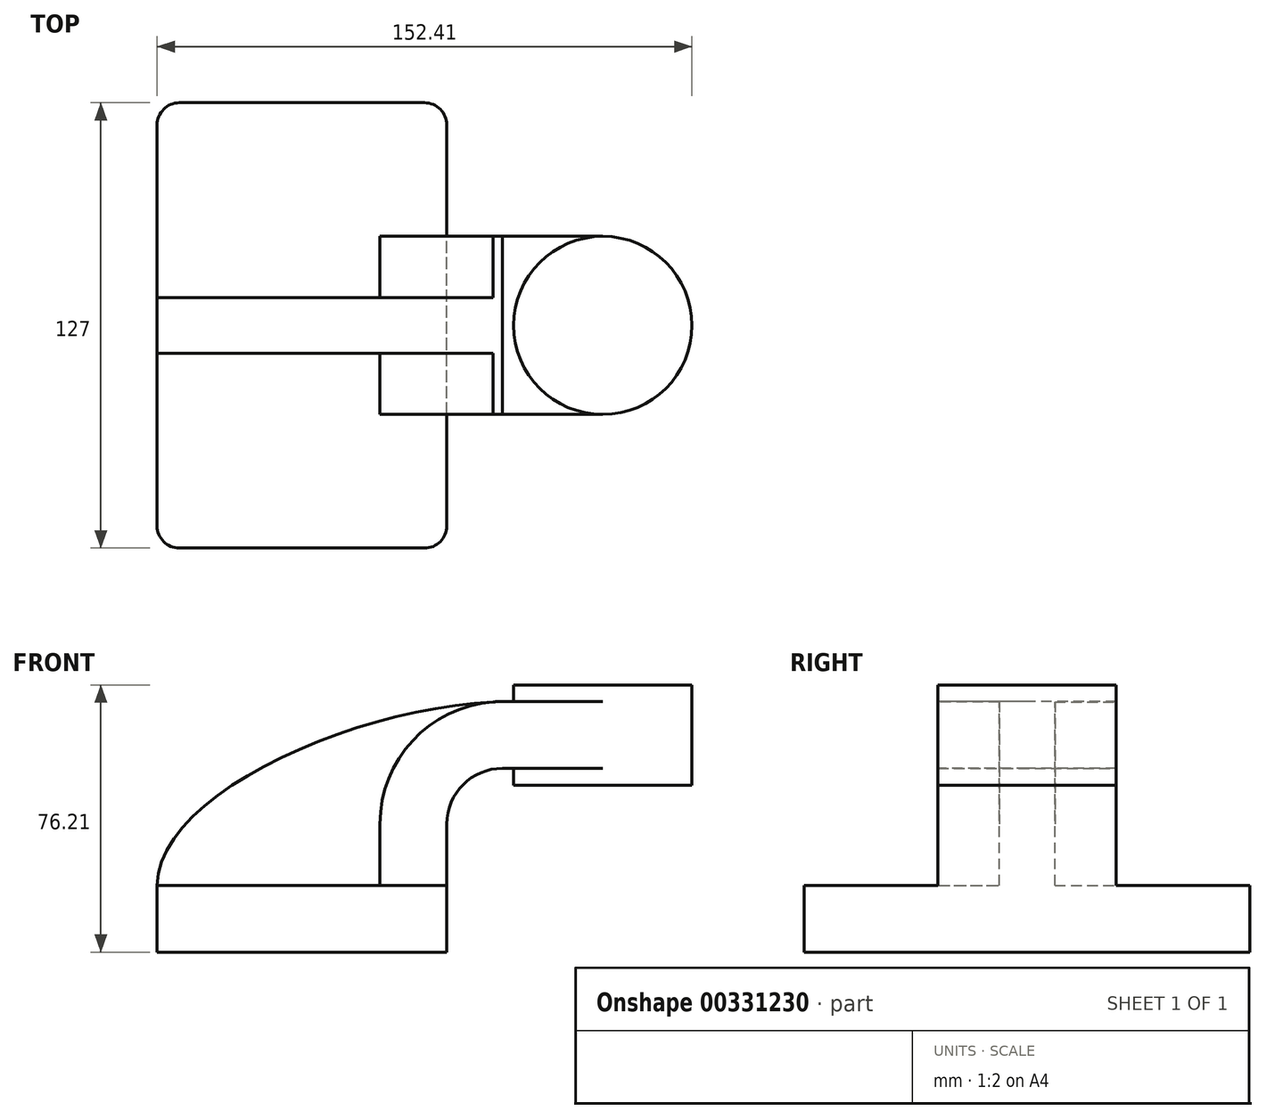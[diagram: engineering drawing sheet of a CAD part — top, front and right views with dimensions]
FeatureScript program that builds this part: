
annotation { "Feature Type Name" : "Feature", "Feature Type Description" : "" }
export const myFeature = defineFeature(function(context is Context, id is Id, definition is map)
    precondition{}
    {
        {
            var Q0;
            Q0=qCreatedBy(makeId("Front.planeOp"),FACE);
            var sketch = newSketch(context, id + "F0", { "sketchPlane" : qUnion([Q0])});
            skLineSegment(sketch, "E0.bottom", {"start": v(-41.27, 9.52) * mm, "end": v(41.28, 9.53) * mm});
            skLineSegment(sketch, "E0.top", {"start": v(-41.27, -9.53) * mm, "end": v(41.28, -9.53) * mm});
            skLineSegment(sketch, "E0.left", {"start": v(-41.28, 9.52) * mm, "end": v(-41.27, -9.53) * mm});
            skLineSegment(sketch, "E0.right", {"start": v(41.27, 9.53) * mm, "end": v(41.28, -9.52) * mm});
            skPoint(sketch, "E0.middle", {"position": v(0, 0) * mm});
            skLineSegment(sketch, "E1", {"start": v(41.27, 9.53) * mm, "end": v(41.27, 27) * mm});
            skLineSegment(sketch, "E2.bottom", {"start": v(60.32, 66.67) * mm, "end": v(111.12, 66.67) * mm});
            skLineSegment(sketch, "E2.top", {"start": v(60.33, 38.1) * mm, "end": v(111.12, 38.1) * mm});
            skLineSegment(sketch, "E2.left", {"start": v(60.32, 66.67) * mm, "end": v(60.33, 38.1) * mm});
            skLineSegment(sketch, "E2.right", {"start": v(111.12, 66.67) * mm, "end": v(111.12, 38.1) * mm});
            skPoint(sketch, "E2.middle", {"position": v(85.72, 52.39) * mm});
            skArc(sketch, "E3", {"start": v(57.15, 42.88) * mm, "mid": v(45.92, 38.23) * mm, "end": v(41.28, 27) * mm});
            skLineSegment(sketch, "E4", {"start": v(57.15, 42.88) * mm, "end": v(85.72, 42.88) * mm});
            skPoint(sketch, "E5", {"position": v(85.72, 38.1) * mm});
            skLineSegment(sketch, "E6.0", {"start": v(57.15, 61.93) * mm, "end": v(85.72, 61.93) * mm});
            skArc(sketch, "E6.1", {"start": v(57.15, 61.93) * mm, "mid": v(32.45, 51.7) * mm, "end": v(22.23, 27) * mm});
            skLineSegment(sketch, "E6.2", {"start": v(22.22, 9.53) * mm, "end": v(22.22, 27) * mm});
            skLineSegment(sketch, "E7", {"start": v(85.72, 38.1) * mm, "end": v(85.72, 66.67) * mm});
            skFitSpline(sketch, "E8", {"points": [v(-41.28, 9.53) * mm, v(57.15, 61.93) * mm], "startDerivative": vector(0.8, 79.7) * mm, "endDerivative": vector(121.44, 3.14) * mm});
            skSolve(sketch);
        }
        {
            var Q0;
            Q0=makeQuery(id+"F0.imprint","IMPRINT",FACE,{"disambiguationData":[TD([[makeQuery(id+"F0.imprint","IMPRINT",EDGE,{"derivedFrom":sQuery(id+"F0.wireOp",EDGE,"E0.top")}),1.0]])]});
            extrude(context, id + "F1", {"entities" : qUnion([Q0]), "endBound" : BoundingType.SYMMETRIC, "depth" : 127 * mm});
        }
        {
            var Q0;
            {var subQ1=sQuery(id+"F0.wireOp",EDGE,"E1");Q0=makeQuery(id+"F0.imprint","IMPRINT",FACE,{"disambiguationData":[TD([[makeQuery(id+"F0.imprint","IMPRINT",EDGE,{"derivedFrom":subQ1}),1.0]])]});}
            var Q1;
            {var subQ0=sQuery(id+"F0.wireOp",EDGE,"E6.0");var subQ1=sQuery(id+"F0.wireOp",EDGE,"E2.left");var subQ2=makeQuery(id+"F0.imprint","INTERSECT",VERTEX,{"derivedFrom":[subQ1,subQ0]});Q1=makeQuery(id+"F0.imprint","IMPRINT",FACE,{"disambiguationData":[TD([[makeQuery(id+"F0.imprint","IMPRINT",EDGE,{"disambiguationData":[TD([[subQ2,-1.0]])],"derivedFrom":subQ1}),1.0]])]});}
            extrude(context, id + "F2", {"entities" : qUnion([Q0, Q1]), "operationType" : NewBodyOperationType.ADD, "endBound" : BoundingType.SYMMETRIC, "depth" : 50.8 * mm});
        }
        {
            var Q0;
            {var subQ3=sQuery(id+"F0.wireOp",EDGE,"E6.2");Q0=makeQuery(id+"F0.imprint","IMPRINT",FACE,{"disambiguationData":[TD([[makeQuery(id+"F0.imprint","IMPRINT",EDGE,{"derivedFrom":subQ3}),1.0]])]});}
            extrude(context, id + "F3", {"entities" : qUnion([Q0]), "operationType" : NewBodyOperationType.ADD, "endBound" : BoundingType.SYMMETRIC, "depth" : 15.88 * mm});
        }
        {
            var Q0;
            {var subQ0=sQuery(id+"F0.wireOp",EDGE,"E2.right");Q0=makeQuery(id+"F0.imprint","IMPRINT",FACE,{"disambiguationData":[TD([[makeQuery(id+"F0.imprint","IMPRINT",EDGE,{"derivedFrom":subQ0}),-1.0]])]});}
            var Q1;
            Q1=sQuery(id+"F0.wireOp",EDGE,"E7");
            revolve(context, id + "F4", {"operationType" : NewBodyOperationType.ADD, "entities" : qUnion([Q0]), "axis" : qUnion([Q1]), "revolveType" : RevolveType.FULL});
        }
        {
            var Q0;
            Q0=makeQuery(id+"F1.opExtrude","CAP_EDGE",EDGE,{"disambiguationData":[OSD([sQuery(id+"F0.wireOp",EDGE,"E0.left")])],"isStart":false});
            var Q1;
            Q1=makeQuery(id+"F1.opExtrude","CAP_EDGE",EDGE,{"disambiguationData":[OSD([sQuery(id+"F0.wireOp",EDGE,"E0.right")])],"isStart":true});
            var Q2;
            Q2=makeQuery(id+"F1.opExtrude","CAP_EDGE",EDGE,{"disambiguationData":[OSD([sQuery(id+"F0.wireOp",EDGE,"E0.right")])],"isStart":false});
            var Q3;
            Q3=makeQuery(id+"F1.opExtrude","CAP_EDGE",EDGE,{"disambiguationData":[OSD([sQuery(id+"F0.wireOp",EDGE,"E0.left")])],"isStart":true});
            fillet(context, id + "F5", {"entities" : qUnion([Q0, Q1, Q2, Q3]), "radius" : 6.35 * mm, "tangentPropagation" : true, "allowEdgeOverflow" : false});
        }
    });
